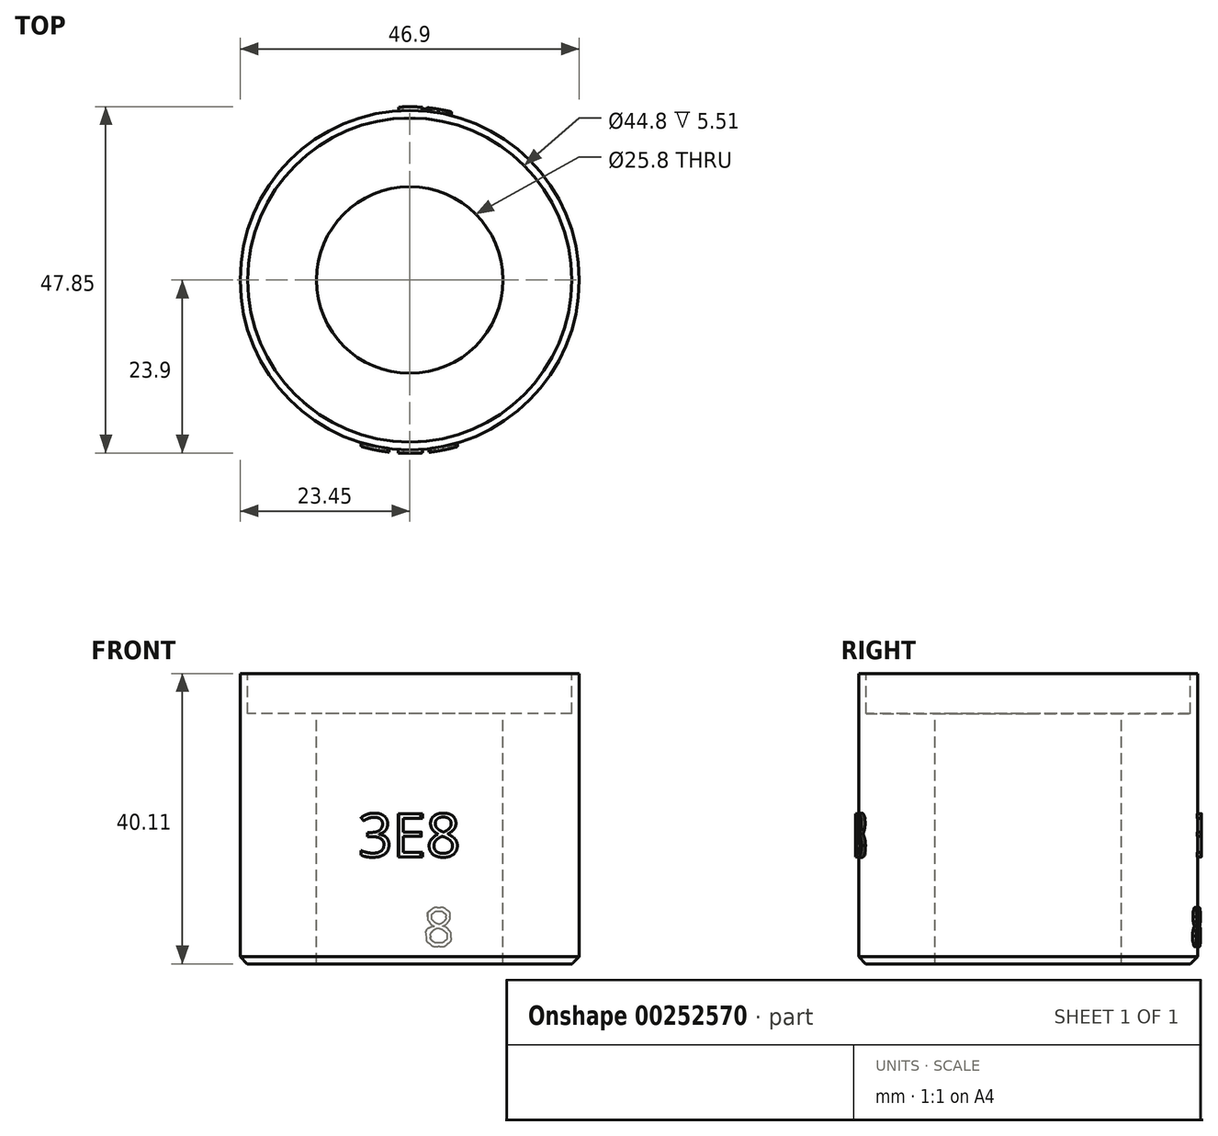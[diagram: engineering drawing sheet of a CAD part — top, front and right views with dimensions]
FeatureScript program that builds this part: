
annotation { "Feature Type Name" : "Feature", "Feature Type Description" : "" }
export const myFeature = defineFeature(function(context is Context, id is Id, definition is map)
    precondition{}
    {
        {
            var Q0;
            Q0=qCreatedBy(makeId("Top.planeOp"),FACE);
            var sketch = newSketch(context, id + "F0", { "sketchPlane" : qUnion([Q0])});
            skCircle(sketch, "E0", {"center": v(0, 0) * mm, "radius": 12.9 * mm});
            skCircle(sketch, "E1", {"center": v(0, 0) * mm, "radius": 23.45 * mm});
            skSolve(sketch);
        }
        {
            assignVariable(context, id + "F1", {"name" : "extend_depth", "anyValue" : 14.71 + 25.4});
        }
        {
            var Q0;
            Q0 = qSketchRegion(id + "F0", true);
            var Q1;
            Q1=makeQuery(id+"F0.imprint","IMPRINT",FACE,{"disambiguationData":[TD([[makeQuery(id+"F0.imprint","IMPRINT",EDGE,{"derivedFrom":sQuery(id+"F0.wireOp",EDGE,"E0")}),1.0]])]});
            extrude(context, id + "F2", {"entities" : qUnion([Q0, Q1]), "depth" : (getVariable(context, 'extend_depth')) * mm});
        }
        {
            var Q0;
            Q0=makeQuery(id+"F2.opExtrude","CAP_FACE",FACE,{"disambiguationData":[OSD([sQuery(id+"F0.wireOp",EDGE,"E1")])],"isStart":false});
            var sketch = newSketch(context, id + "F3", { "sketchPlane" : qUnion([Q0])});
            skCircle(sketch, "E2", {"center": v(0, 0) * mm, "radius": 22.4 * mm});
            skSolve(sketch);
        }
        {
            var Q0;
            Q0 = qSketchRegion(id + "F3", true);
            extrude(context, id + "F4", {"entities" : qUnion([Q0]), "operationType" : NewBodyOperationType.REMOVE, "oppositeDirection" : true, "depth" : 5.5 * mm});
        }
        {
            var Q0;
            Q0=makeQuery(id+"F4.boolean.opBoolean","COPY",FACE,{"derivedFrom":makeQuery(id+"F4.opExtrude","CAP_FACE",FACE,{"disambiguationData":[OSD([sQuery(id+"F3.wireOp",EDGE,"E2")])],"isStart":false})});
            var sketch = newSketch(context, id + "F5", { "sketchPlane" : qUnion([Q0])});
            skCircle(sketch, "E3.0", {"center": v(0, 0) * mm, "radius": 12.9 * mm});
            skSolve(sketch);
        }
        {
            var Q0;
            Q0 = qSketchRegion(id + "F5", true);
            extrude(context, id + "F6", {"entities" : qUnion([Q0]), "operationType" : NewBodyOperationType.REMOVE, "endBound" : BoundingType.THROUGH_ALL, "oppositeDirection" : true, "depth" : 25 * mm});
        }
        {
            var Q0;
            Q0=makeQuery(id+"F2.opExtrude","CAP_EDGE",EDGE,{"disambiguationData":[OSD([sQuery(id+"F0.wireOp",EDGE,"E1")])],"isStart":true});
            var Q1;
            Q1=makeQuery(id+"F6.boolean.opBoolean","COPY",EDGE,{"derivedFrom":makeQuery(id+"F6.opExtrude","CAP_EDGE",EDGE,{"disambiguationData":[OSD([sQuery(id+"F5.wireOp",EDGE,"E3.0")])],"isStart":true})});
            chamfer(context, id + "F7", {"entities" : qUnion([Q0, Q1]), "width" : 1 * mm, "tangentPropagation" : true});
        }
        {
            var Q0;
            Q0=qCreatedBy(makeId("Front.planeOp"),FACE);
            cPlane(context, id + "F8", {"entities" : qUnion([Q0]), "cplaneType" : CPlaneType.OFFSET, "offset" : 23.9 * mm, "width" : 150 * mm, "height" : 150 * mm});
        }
        {
            var Q0;
            Q0=qCreatedBy(id+"F8.planeOp",FACE);
            var sketch = newSketch(context, id + "F9", { "sketchPlane" : qUnion([Q0])});
            skLineSegment(sketch, "E4.0.0", {"start": v(-22.4, 34.6) * mm, "end": v(22.4, 34.6) * mm, "construction": true});
            skText(sketch, "E5", { "text": "3E8", "fontName": "OpenSans-Regular.ttf"});
            skLineSegment(sketch, "E6.0", {"start": v(-23.45, 1) * mm, "end": v(23.45, 1) * mm, "construction": true});
            skLineSegment(sketch, "E7", {"start": v(0, 34.6) * mm, "end": v(0, 1) * mm, "construction": true});
            skPoint(sketch, "E8", {"position": v(0, 17.8) * mm});
            const initialGuessF9  = {"E5": [-0.00714, 0.0148, 1, 0, 0.006]};
            skSetInitialGuess(sketch, initialGuessF9);
            skSolve(sketch);
        }
        {
            var Q0;
            Q0=makeQuery(id+"F2.opExtrude","CAP_FACE",FACE,{"disambiguationData":[OSD([sQuery(id+"F0.wireOp",EDGE,"E1")])],"isStart":false});
            var sketch = newSketch(context, id + "F10", { "sketchPlane" : qUnion([Q0])});
            skCircle(sketch, "E9.0", {"center": v(0, 0) * mm, "radius": 23.45 * mm, "construction": true});
            skCircle(sketch, "E10.0", {"center": v(0, 0) * mm, "radius": 23.95 * mm});
            skCircle(sketch, "E11.0", {"center": v(0, 0) * mm, "radius": 28.95 * mm});
            skSolve(sketch);
        }
        {
            var Q0;
            Q0=qCreatedBy(makeId("Front.planeOp"),FACE);
            cPlane(context, id + "F11", {"entities" : qUnion([Q0]), "cplaneType" : CPlaneType.OFFSET, "offset" : 25 * mm, "oppositeDirection" : true, "width" : 150 * mm, "height" : 150 * mm});
        }
        {
            var Q0;
            Q0=qCreatedBy(id+"F11.planeOp",FACE);
            var sketch = newSketch(context, id + "F12", { "sketchPlane" : qUnion([Q0])});
            skFitSpline(sketch, "E12.0.0", {"points": [v(4.02, 7.73) * mm, v(3.33, 7.73) * mm, v(2.91, 7.4) * mm]});
            skFitSpline(sketch, "E12.0.1", {"points": [v(2.91, 7.4) * mm, v(2.5, 7.06) * mm, v(2.5, 6.5) * mm]});
            skFitSpline(sketch, "E12.0.2", {"points": [v(2.5, 6.5) * mm, v(2.5, 6.1) * mm, v(2.7, 5.79) * mm]});
            skFitSpline(sketch, "E12.0.3", {"points": [v(2.7, 5.79) * mm, v(2.92, 5.47) * mm, v(3.4, 5.2) * mm]});
            skFitSpline(sketch, "E12.0.4", {"points": [v(3.4, 5.2) * mm, v(2.33, 4.7) * mm, v(2.33, 3.82) * mm]});
            skFitSpline(sketch, "E12.0.5", {"points": [v(2.33, 3.82) * mm, v(2.33, 3.15) * mm, v(2.77, 2.8) * mm]});
            skFitSpline(sketch, "E12.0.6", {"points": [v(2.77, 2.8) * mm, v(3.22, 2.43) * mm, v(4.04, 2.43) * mm]});
            skFitSpline(sketch, "E12.0.7", {"points": [v(4.04, 2.43) * mm, v(4.82, 2.43) * mm, v(5.27, 2.81) * mm]});
            skFitSpline(sketch, "E12.0.8", {"points": [v(5.27, 2.81) * mm, v(5.72, 3.2) * mm, v(5.72, 3.84) * mm]});
            skFitSpline(sketch, "E12.0.9", {"points": [v(5.72, 3.84) * mm, v(5.72, 4.27) * mm, v(5.45, 4.6) * mm]});
            skFitSpline(sketch, "E12.0.10", {"points": [v(5.45, 4.6) * mm, v(5.19, 4.93) * mm, v(4.56, 5.23) * mm]});
            skFitSpline(sketch, "E12.0.11", {"points": [v(4.56, 5.23) * mm, v(5.08, 5.49) * mm, v(5.31, 5.8) * mm]});
            skFitSpline(sketch, "E12.0.12", {"points": [v(5.31, 5.8) * mm, v(5.55, 6.11) * mm, v(5.55, 6.5) * mm]});
            skFitSpline(sketch, "E12.0.13", {"points": [v(5.55, 6.5) * mm, v(5.55, 7.07) * mm, v(5.14, 7.4) * mm]});
            skFitSpline(sketch, "E12.0.14", {"points": [v(5.14, 7.4) * mm, v(4.73, 7.73) * mm, v(4.02, 7.73) * mm]});
            skLineSegment(sketch, "E13.0.0", {"start": v(1.76, 14.8) * mm, "end": v(1.76, 15.42) * mm});
            skLineSegment(sketch, "E13.0.1", {"start": v(1.76, 15.42) * mm, "end": v(-0.86, 15.42) * mm});
            skLineSegment(sketch, "E13.0.2", {"start": v(-0.86, 15.42) * mm, "end": v(-0.86, 17.6) * mm});
            skLineSegment(sketch, "E13.0.3", {"start": v(-0.86, 17.6) * mm, "end": v(1.6, 17.6) * mm});
            skLineSegment(sketch, "E13.0.4", {"start": v(1.6, 17.6) * mm, "end": v(1.6, 18.22) * mm});
            skLineSegment(sketch, "E13.0.5", {"start": v(1.6, 18.22) * mm, "end": v(-0.86, 18.22) * mm});
            skLineSegment(sketch, "E13.0.6", {"start": v(-0.86, 18.22) * mm, "end": v(-0.86, 20.13) * mm});
            skLineSegment(sketch, "E13.0.7", {"start": v(-0.86, 20.13) * mm, "end": v(1.76, 20.13) * mm});
            skLineSegment(sketch, "E13.0.8", {"start": v(1.76, 20.13) * mm, "end": v(1.76, 20.75) * mm});
            skLineSegment(sketch, "E13.0.9", {"start": v(1.76, 20.75) * mm, "end": v(-1.55, 20.75) * mm});
            skLineSegment(sketch, "E13.0.10", {"start": v(-1.55, 20.75) * mm, "end": v(-1.55, 14.8) * mm});
            skLineSegment(sketch, "E13.0.11", {"start": v(-1.55, 14.8) * mm, "end": v(1.76, 14.8) * mm});
            skFitSpline(sketch, "E14.0.0", {"points": [v(-2.64, 6.44) * mm, v(-2.64, 7.04) * mm, v(-3.05, 7.39) * mm]});
            skFitSpline(sketch, "E14.0.1", {"points": [v(-3.05, 7.39) * mm, v(-3.47, 7.73) * mm, v(-4.22, 7.73) * mm]});
            skFitSpline(sketch, "E14.0.2", {"points": [v(-4.22, 7.73) * mm, v(-4.68, 7.73) * mm, v(-5.1, 7.59) * mm]});
            skFitSpline(sketch, "E14.0.3", {"points": [v(-5.1, 7.59) * mm, v(-5.5, 7.44) * mm, v(-5.82, 7.2) * mm]});
            skLineSegment(sketch, "E14.0.4", {"start": v(-6.72, 20.22) * mm, "end": v(-6.38, 19.76) * mm});
            skFitSpline(sketch, "E14.0.5", {"points": [v(-5.53, 6.8) * mm, v(-5.14, 7.05) * mm, v(-4.84, 7.14) * mm]});
            skFitSpline(sketch, "E14.0.6", {"points": [v(-4.84, 7.14) * mm, v(-4.54, 7.23) * mm, v(-4.2, 7.23) * mm]});
            skFitSpline(sketch, "E14.0.7", {"points": [v(-4.2, 7.23) * mm, v(-3.76, 7.23) * mm, v(-3.5, 7.01) * mm]});
            skFitSpline(sketch, "E14.0.8", {"points": [v(-3.5, 7.01) * mm, v(-3.24, 6.8) * mm, v(-3.24, 6.42) * mm]});
            skFitSpline(sketch, "E14.0.9", {"points": [v(-3.24, 6.42) * mm, v(-3.24, 5.95) * mm, v(-3.6, 5.68) * mm]});
            skFitSpline(sketch, "E14.0.10", {"points": [v(-3.6, 5.68) * mm, v(-3.95, 5.42) * mm, v(-4.55, 5.42) * mm]});
            skLineSegment(sketch, "E14.0.11", {"start": v(-5.25, 18.16) * mm, "end": v(-5.85, 18.16) * mm});
            skLineSegment(sketch, "E14.0.12", {"start": v(-5.85, 18.16) * mm, "end": v(-5.85, 17.58) * mm});
            skLineSegment(sketch, "E14.0.13", {"start": v(-5.85, 17.58) * mm, "end": v(-5.26, 17.58) * mm});
            skFitSpline(sketch, "E14.0.14", {"points": [v(-4.56, 4.91) * mm, v(-3.08, 4.91) * mm, v(-3.08, 3.97) * mm]});
            skFitSpline(sketch, "E14.0.15", {"points": [v(-3.08, 3.97) * mm, v(-3.08, 2.93) * mm, v(-4.42, 2.93) * mm]});
            skFitSpline(sketch, "E14.0.16", {"points": [v(-4.42, 2.93) * mm, v(-4.76, 2.93) * mm, v(-5.14, 3.01) * mm]});
            skFitSpline(sketch, "E14.0.17", {"points": [v(-5.14, 3.01) * mm, v(-5.52, 3.1) * mm, v(-5.85, 3.27) * mm]});
            skLineSegment(sketch, "E14.0.18", {"start": v(-6.75, 15.68) * mm, "end": v(-6.75, 15.04) * mm});
            skFitSpline(sketch, "E14.0.19", {"points": [v(-5.85, 2.7) * mm, v(-5.53, 2.55) * mm, v(-5.2, 2.5) * mm]});
            skFitSpline(sketch, "E14.0.20", {"points": [v(-5.2, 2.5) * mm, v(-4.85, 2.43) * mm, v(-4.44, 2.43) * mm]});
            skFitSpline(sketch, "E14.0.21", {"points": [v(-4.44, 2.43) * mm, v(-3.5, 2.43) * mm, v(-2.99, 2.83) * mm]});
            skFitSpline(sketch, "E14.0.22", {"points": [v(-2.99, 2.83) * mm, v(-2.48, 3.22) * mm, v(-2.48, 3.96) * mm]});
            skFitSpline(sketch, "E14.0.23", {"points": [v(-2.48, 3.96) * mm, v(-2.48, 4.47) * mm, v(-2.78, 4.8) * mm]});
            skFitSpline(sketch, "E14.0.24", {"points": [v(-2.78, 4.8) * mm, v(-3.08, 5.11) * mm, v(-3.7, 5.19) * mm]});
            skLineSegment(sketch, "E14.0.25", {"start": v(-4.27, 17.9) * mm, "end": v(-4.27, 17.93) * mm});
            skFitSpline(sketch, "E14.0.26", {"points": [v(-3.7, 5.22) * mm, v(-3.2, 5.32) * mm, v(-2.91, 5.63) * mm]});
            skFitSpline(sketch, "E14.0.27", {"points": [v(-2.91, 5.63) * mm, v(-2.64, 5.95) * mm, v(-2.64, 6.44) * mm]});
            skFitSpline(sketch, "E15.0.0", {"points": [v(3.9, 4.95) * mm, v(3.38, 4.73) * mm, v(3.14, 4.46) * mm]});
            skFitSpline(sketch, "E15.0.1", {"points": [v(3.14, 4.46) * mm, v(2.9, 4.18) * mm, v(2.9, 3.8) * mm]});
            skFitSpline(sketch, "E15.0.2", {"points": [v(2.9, 3.8) * mm, v(2.9, 3.38) * mm, v(3.2, 3.14) * mm]});
            skFitSpline(sketch, "E15.0.3", {"points": [v(3.2, 3.14) * mm, v(3.5, 2.9) * mm, v(4.03, 2.9) * mm]});
            skFitSpline(sketch, "E15.0.4", {"points": [v(4.03, 2.9) * mm, v(4.55, 2.9) * mm, v(4.85, 3.15) * mm]});
            skFitSpline(sketch, "E15.0.5", {"points": [v(4.85, 3.15) * mm, v(5.14, 3.4) * mm, v(5.14, 3.83) * mm]});
            skFitSpline(sketch, "E15.0.6", {"points": [v(5.14, 3.83) * mm, v(5.14, 4.17) * mm, v(4.86, 4.44) * mm]});
            skFitSpline(sketch, "E15.0.7", {"points": [v(4.86, 4.44) * mm, v(4.59, 4.7) * mm, v(3.9, 4.95) * mm]});
            skFitSpline(sketch, "E16.0.0", {"points": [v(4.97, 6.48) * mm, v(4.97, 6.83) * mm, v(4.72, 7.04) * mm]});
            skFitSpline(sketch, "E16.0.1", {"points": [v(4.72, 7.04) * mm, v(4.46, 7.25) * mm, v(4.01, 7.25) * mm]});
            skFitSpline(sketch, "E16.0.2", {"points": [v(4.01, 7.25) * mm, v(3.57, 7.25) * mm, v(3.32, 7.04) * mm]});
            skFitSpline(sketch, "E16.0.3", {"points": [v(3.32, 7.04) * mm, v(3.07, 6.83) * mm, v(3.07, 6.48) * mm]});
            skFitSpline(sketch, "E16.0.4", {"points": [v(3.07, 6.48) * mm, v(3.07, 6.15) * mm, v(3.28, 5.92) * mm]});
            skFitSpline(sketch, "E16.0.5", {"points": [v(3.28, 5.92) * mm, v(3.49, 5.69) * mm, v(4.05, 5.46) * mm]});
            skFitSpline(sketch, "E16.0.6", {"points": [v(4.05, 5.46) * mm, v(4.55, 5.67) * mm, v(4.76, 5.91) * mm]});
            skFitSpline(sketch, "E16.0.7", {"points": [v(4.76, 5.91) * mm, v(4.97, 6.15) * mm, v(4.97, 6.48) * mm]});
            skSolve(sketch);
        }
        {
            var Q0;
            Q0=makeQuery(id+"F12.imprint","IMPRINT",FACE,{"disambiguationData":[TD([[makeQuery(id+"F12.imprint","IMPRINT",EDGE,{"derivedFrom":sQuery(id+"F12.wireOp",EDGE,"E12.0.0")}),1.0]])]});
            var Q1;
            Q1=makeQuery(id+"F12.imprint","IMPRINT",FACE,{"disambiguationData":[TD([[makeQuery(id+"F12.imprint","IMPRINT",EDGE,{"derivedFrom":sQuery(id+"F12.wireOp",EDGE,"E13.0.0")}),1.0]])]});
            var Q2;
            Q2=makeQuery(id+"F12.imprint","IMPRINT",FACE,{"disambiguationData":[TD([[makeQuery(id+"F12.imprint","IMPRINT",EDGE,{"derivedFrom":sQuery(id+"F12.wireOp",EDGE,"E14.0.0")}),1.0]])]});
            var Q3;
            {var subQ0=sQuery(id+"F0.wireOp",EDGE,"E1");Q3=makeQuery(id+"F14.boolean.opBoolean","SPLIT",FACE,{"disambiguationData":[TD([makeQuery(id+"F2.opExtrude","CAP_FACE",FACE,{"disambiguationData":[OSD([subQ0])],"isStart":false})])],"derivedFrom":makeQuery(id+"F2.opExtrude","SWEPT_FACE",FACE,{"disambiguationData":[OSD([subQ0])]})});}
            extrude(context, id + "F13", {"entities" : qUnion([Q0, Q1, Q2]), "operationType" : NewBodyOperationType.ADD, "endBound" : BoundingType.UP_TO_SURFACE, "endBoundEntityFace" : qUnion([Q3]), "depth" : 25 * mm});
        }
        {
            var Q0;
            Q0 = qSketchRegion(id + "F9", true);
            var Q1;
            Q1=makeQuery(id+"F2.opExtrude","SWEPT_FACE",FACE,{"disambiguationData":[OSD([sQuery(id+"F0.wireOp",EDGE,"E1")])]});
            extrude(context, id + "F14", {"entities" : qUnion([Q0]), "operationType" : NewBodyOperationType.ADD, "endBound" : BoundingType.UP_TO_SURFACE, "oppositeDirection" : true, "endBoundEntityFace" : qUnion([Q1]), "depth" : 25 * mm});
        }
        {
            var Q0;
            Q0 = qSketchRegion(id + "F10", true);
            extrude(context, id + "F15", {"entities" : qUnion([Q0]), "operationType" : NewBodyOperationType.REMOVE, "endBound" : BoundingType.THROUGH_ALL, "oppositeDirection" : true, "depth" : 25 * mm});
        }
    });
